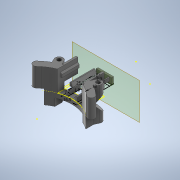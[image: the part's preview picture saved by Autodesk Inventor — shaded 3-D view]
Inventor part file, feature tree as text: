
AUTODESK INVENTOR PART (.ipt)
format: ipt  version: 2020 (Build 240168000, 168)  size: 680,448 bytes
history: native  units: mm
features: sketch x13, extrude x12, projected_geometry x10, other x3, sweep x1
ambient origin geometry x8: Origin, YZ Plane, XZ Plane, XY Plane, X Axis, Y Axis, Z Axis, Center Point
bodies: Body1 (feature_tree), Body2 (feature_tree), Body3 (feature_tree), Body4 (feature_tree)
feature tree (39):
  other  "Твердое тело1"
  extrude  "Выдавливание1"  Depth=35.0mm TaperAngle=0.0deg
  sketch  "Эскиз2"
  extrude  "Выдавливание2"  Depth=4.0mm
  sweep  "Сдвиг1"
  extrude  "Выдавливание5"  Depth=8.0mm
  extrude  "Выдавливание6"  Depth=35.0mm TaperAngle=0.0deg
  extrude  "Выдавливание7"  Depth=8.5mm
  extrude  "Выдавливание8"  TaperAngle=45.0deg  [1 undecoded]
  other  "РабПлоскость1"
  extrude  "Выдавливание9"  Depth=8.5mm
  extrude  "Выдавливание10"  TaperAngle=45.0deg  [1 undecoded]
  extrude  "Выдавливание11"  TaperAngle=0.0deg  [1 undecoded]
  sketch  "Эскиз14"
  extrude  "Выдавливание13"  Depth=15.0mm TaperAngle=0.0deg
  other  "РабПлоскость2"
  extrude  "Выдавливание14"  Depth=5.0mm TaperAngle=0.0deg
  extrude  "Выдавливание15"  Depth=15.0mm TaperAngle=0.0deg
  sketch  "Эскиз17"
  sketch  "Эскиз1"
  sketch  "Эскиз3"
  projected_geometry  "Спроецированная петля1"
  projected_geometry  "Спроецированная петля2"
  sketch  "3D эскиз1"
  sketch  "Эскиз4"
  sketch  "Эскиз6"
  projected_geometry  "Спроецированная петля4"
  sketch  "Эскиз7"
  projected_geometry  "Спроецированная петля5"
  sketch  "Эскиз9"
  projected_geometry  "Спроецированная петля7"
  sketch  "Эскиз11"
  projected_geometry  "Спроецированная петля8"
  sketch  "Эскиз12"
  projected_geometry  "Спроецированная петля9"
  projected_geometry  "Спроецированная петля10"
  sketch  "Эскиз16"
  projected_geometry  "Спроецированная петля15"
  projected_geometry  "Спроецированная петля16"
note: 3 required parameter values undecoded (feature->parameter linkage not recoverable at this tier; creation-order binding heuristic only, values carry confidence <= 0.55)
